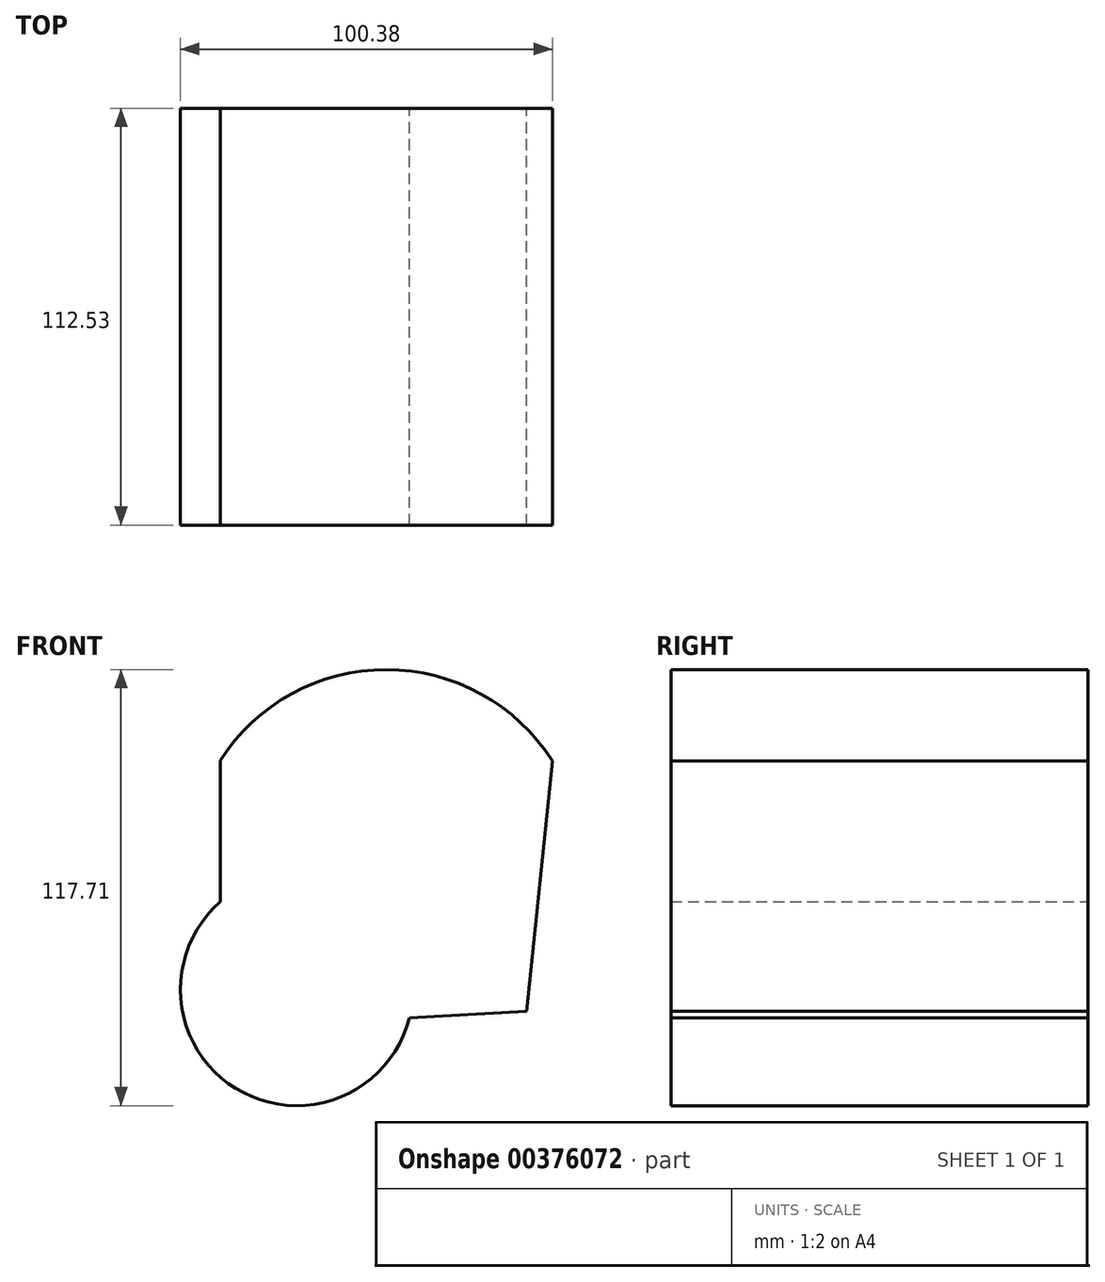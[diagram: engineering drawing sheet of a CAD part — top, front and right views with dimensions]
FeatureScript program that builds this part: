
annotation { "Feature Type Name" : "Feature", "Feature Type Description" : "" }
export const myFeature = defineFeature(function(context is Context, id is Id, definition is map)
    precondition{}
    {
        {
            var Q0;
            Q0=qCreatedBy(makeId("Front.planeOp"),FACE);
            var sketch = newSketch(context, id + "F0", { "sketchPlane" : qUnion([Q0])});
            skArc(sketch, "E0", {"start": v(45.42, 37.16) * mm, "mid": v(0.64, 61.82) * mm, "end": v(-44.22, 37.3) * mm});
            skLineSegment(sketch, "E1", {"start": v(-44.22, 37.3) * mm, "end": v(-44.22, -35.17) * mm});
            skLineSegment(sketch, "E2", {"start": v(-44.22, -35.17) * mm, "end": v(38.5, -30.37) * mm});
            skLineSegment(sketch, "E3", {"start": v(38.5, -30.37) * mm, "end": v(45.42, 37.16) * mm});
            skCircle(sketch, "E4", {"center": v(50.35, -55.01) * mm, "radius": 20.93 * mm});
            skCircle(sketch, "E5", {"center": v(-23.58, -24.5) * mm, "radius": 31.38 * mm});
            skSolve(sketch);
        }
        {
            var Q0;
            {var subQ5=sQuery(id+"F0.wireOp",EDGE,"E0");Q0=makeQuery(id+"F0.imprint","IMPRINT",FACE,{"disambiguationData":[TD([[makeQuery(id+"F0.imprint","IMPRINT",EDGE,{"derivedFrom":subQ5}),1.0]])]});}
            var Q1;
            {var subQ0=sQuery(id+"F0.wireOp",EDGE,"E2");var subQ1=sQuery(id+"F0.wireOp",EDGE,"E1");var subQ2=makeQuery(id+"F0.imprint","INTERSECT",VERTEX,{"derivedFrom":[subQ1,subQ0]});Q1=makeQuery(id+"F0.imprint","IMPRINT",FACE,{"disambiguationData":[TD([[makeQuery(id+"F0.imprint","IMPRINT",EDGE,{"disambiguationData":[TD([[subQ2,1.0]])],"derivedFrom":subQ1}),1.0]])]});}
            var Q2;
            {var subQ0=sQuery(id+"F0.wireOp",EDGE,"E2");var subQ1=sQuery(id+"F0.wireOp",EDGE,"E1");var subQ2=makeQuery(id+"F0.imprint","INTERSECT",VERTEX,{"derivedFrom":[subQ1,subQ0]});Q2=makeQuery(id+"F0.imprint","IMPRINT",FACE,{"disambiguationData":[TD([[makeQuery(id+"F0.imprint","IMPRINT",EDGE,{"disambiguationData":[TD([[subQ2,1.0]])],"derivedFrom":subQ1}),-1.0]])]});}
            extrude(context, id + "F1", {"entities" : qUnion([Q0, Q1, Q2]), "depth" : 112.53 * mm});
        }
    });
